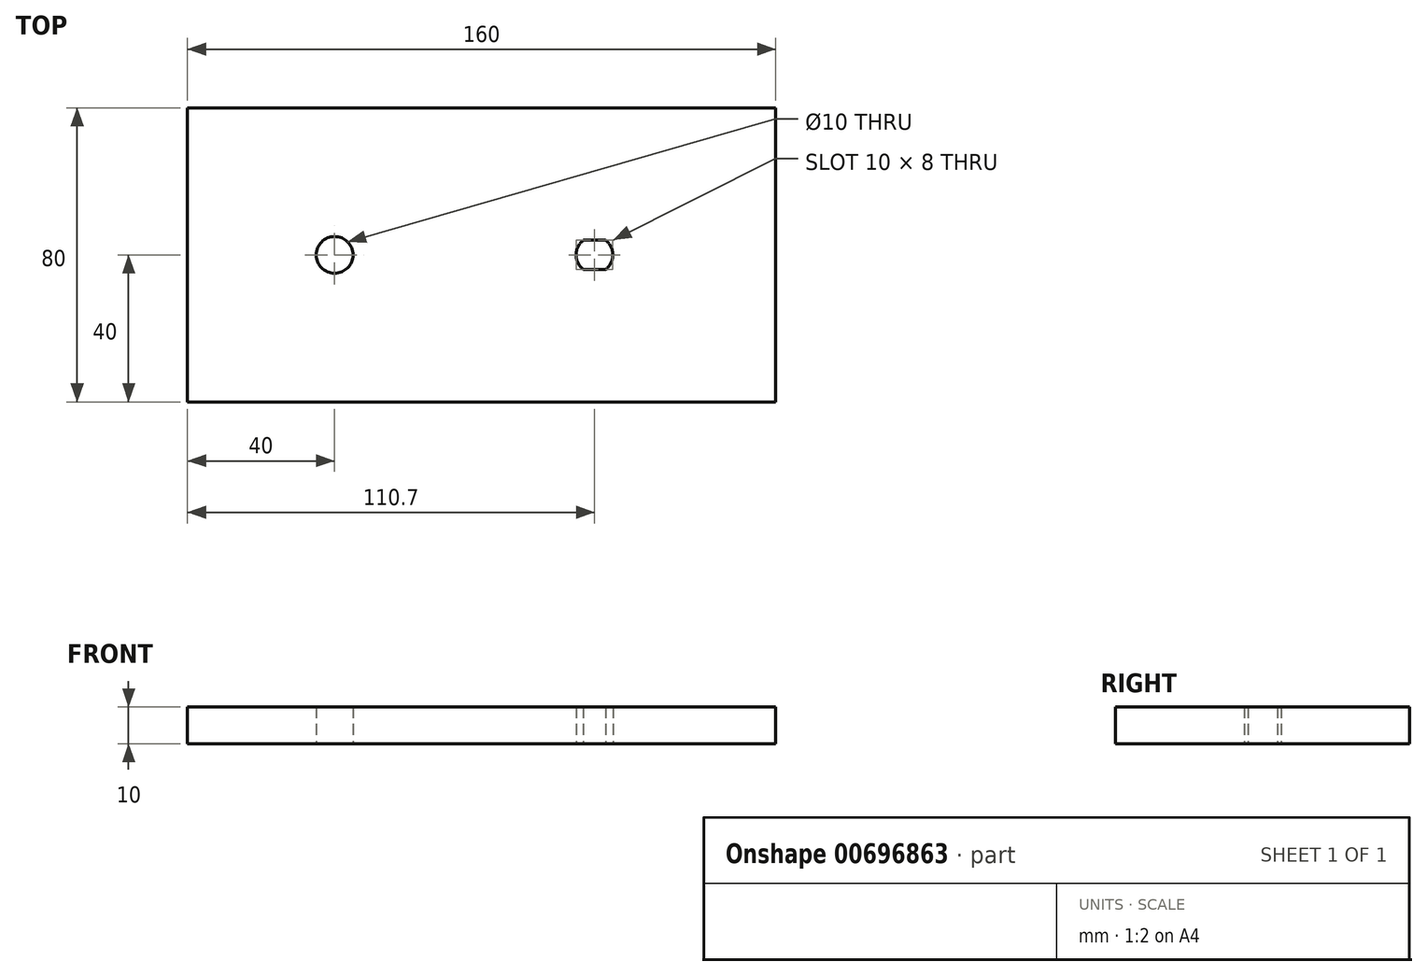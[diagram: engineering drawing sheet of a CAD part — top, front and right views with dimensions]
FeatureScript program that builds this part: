
annotation { "Feature Type Name" : "Feature", "Feature Type Description" : "" }
export const myFeature = defineFeature(function(context is Context, id is Id, definition is map)
    precondition{}
    {
        {
            var Q0;
            Q0=qCreatedBy(makeId("Top.planeOp"),FACE);
            var sketch = newSketch(context, id + "F0", { "sketchPlane" : qUnion([Q0])});
            skLineSegment(sketch, "E0.bottom", {"start": v(0, 0) * mm, "end": v(160, 0) * mm});
            skLineSegment(sketch, "E0.top", {"start": v(0, 80) * mm, "end": v(160, 80) * mm});
            skLineSegment(sketch, "E0.left", {"start": v(0, 0) * mm, "end": v(0, 80) * mm});
            skLineSegment(sketch, "E0.right", {"start": v(160, 0) * mm, "end": v(160, 80) * mm});
            skLineSegment(sketch, "E1", {"start": v(0, 40) * mm, "end": v(160, 40) * mm, "construction": true});
            skCircle(sketch, "E2", {"center": v(40, 40) * mm, "radius": 5 * mm});
            skArc(sketch, "E3", {"start": v(113.7, 36) * mm, "mid": v(115.7, 40) * mm, "end": v(113.7, 44) * mm});
            skLineSegment(sketch, "E4", {"start": v(107.7, 44) * mm, "end": v(113.7, 44) * mm});
            skLineSegment(sketch, "E5", {"start": v(107.7, 36) * mm, "end": v(113.7, 36) * mm});
            skArc(sketch, "E6.trimOffspring", {"start": v(107.7, 44) * mm, "mid": v(105.7, 40) * mm, "end": v(107.7, 36) * mm});
            skSolve(sketch);
        }
        {
            var Q0;
            Q0=makeQuery(id+"F0.imprint","IMPRINT",FACE,{"disambiguationData":[TD([[makeQuery(id+"F0.imprint","IMPRINT",EDGE,{"derivedFrom":sQuery(id+"F0.wireOp",EDGE,"E0.bottom")}),1.0]])]});
            extrude(context, id + "F1", {"entities" : qUnion([Q0]), "depth" : 10 * mm, "offsetDistance" : 25 * mm});
        }
    });
